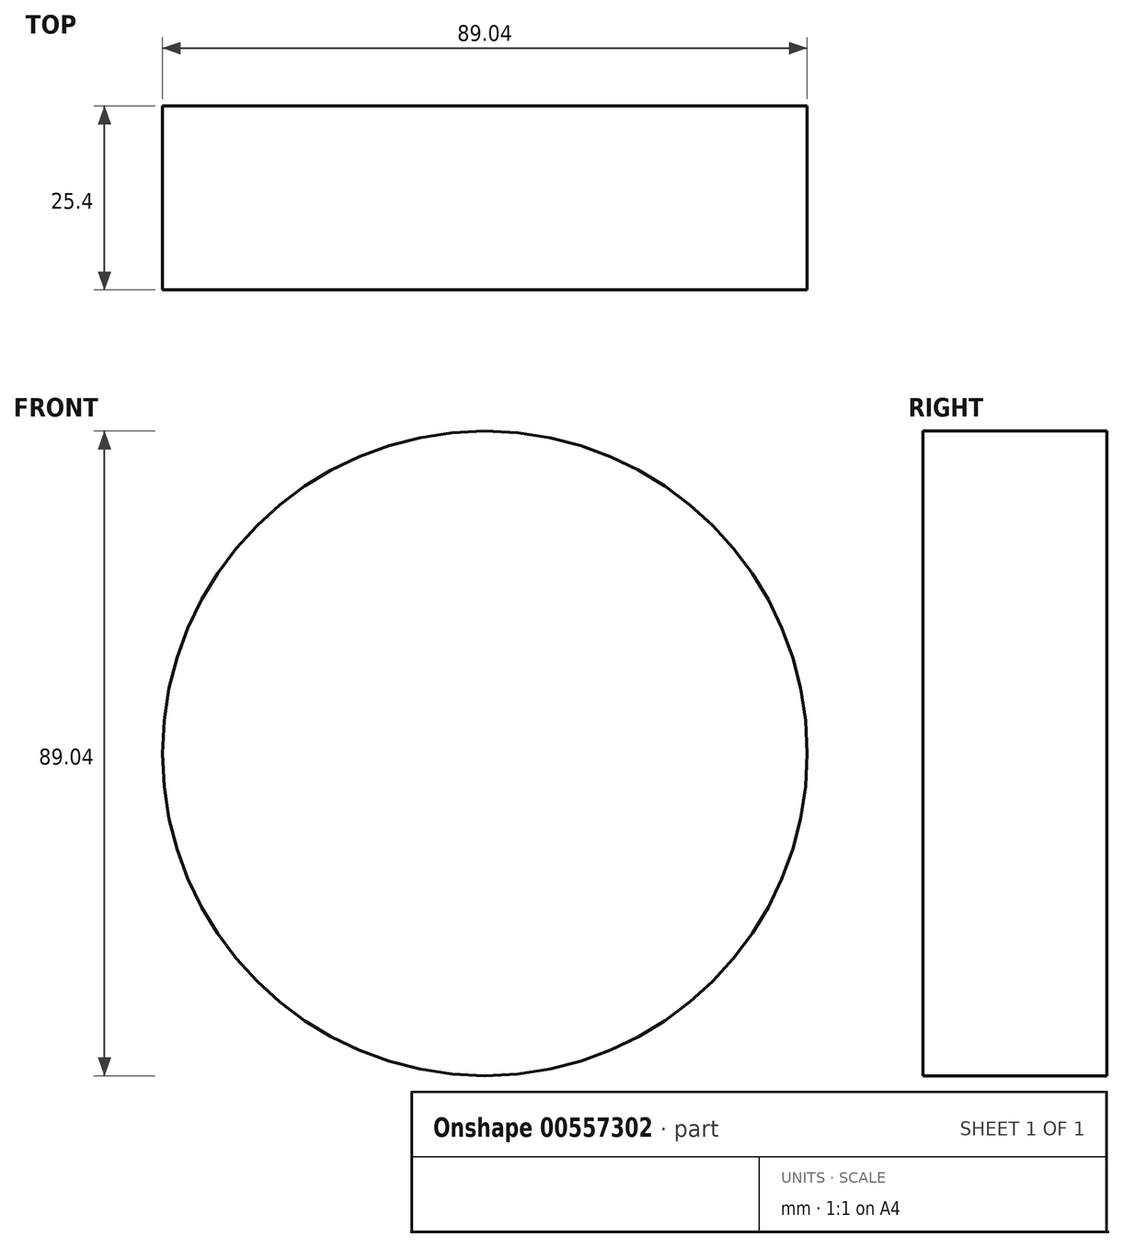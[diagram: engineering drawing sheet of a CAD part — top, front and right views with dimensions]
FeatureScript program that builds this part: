
annotation { "Feature Type Name" : "Feature", "Feature Type Description" : "" }
export const myFeature = defineFeature(function(context is Context, id is Id, definition is map)
    precondition{}
    {
        {
            var Q0;
            Q0=qCreatedBy(makeId("Front.planeOp"),FACE);
            var sketch = newSketch(context, id + "F0", { "sketchPlane" : qUnion([Q0])});
            skCircle(sketch, "E0", {"center": v(0, 0) * mm, "radius": 44.52 * mm});
            skSolve(sketch);
        }
        {
            var Q0;
            Q0=sQuery(id+"F0.wireOp",EDGE,"E0");
            extrude(context, id + "F1", {"bodyType" : ToolBodyType.SURFACE, "surfaceEntities" : qUnion([Q0]), "depth" : 25.4 * mm, "offsetDistance" : 25.4 * mm});
        }
    });
